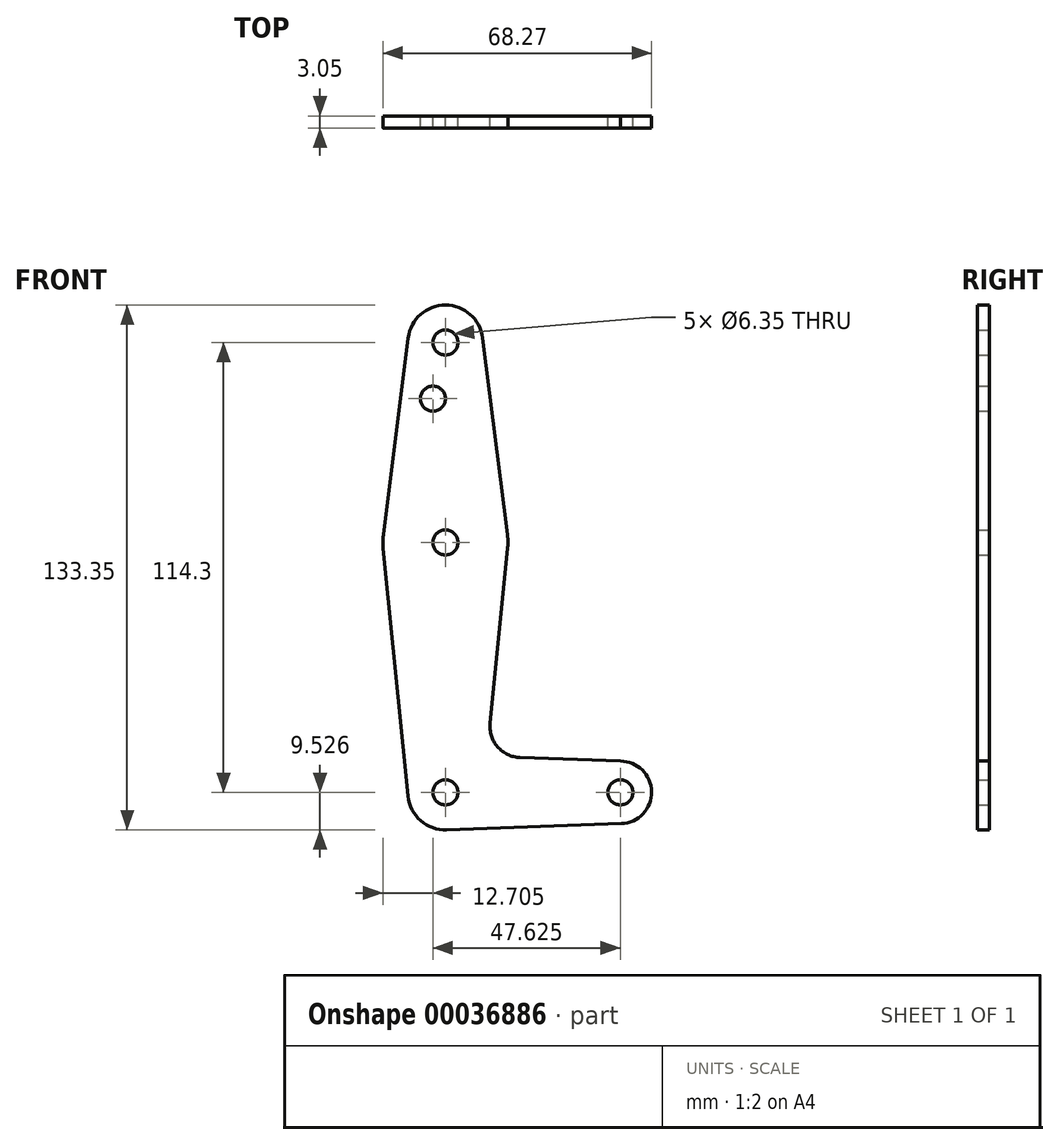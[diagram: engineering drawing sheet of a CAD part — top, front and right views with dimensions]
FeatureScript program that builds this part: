
annotation { "Feature Type Name" : "Feature", "Feature Type Description" : "" }
export const myFeature = defineFeature(function(context is Context, id is Id, definition is map)
    precondition{}
    {
        {
            var Q0;
            Q0=qCreatedBy(makeId("Front.planeOp"),FACE);
            var sketch = newSketch(context, id + "F0", { "sketchPlane" : qUnion([Q0])});
            skLineSegment(sketch, "E0", {"start": v(-44.45, 62.85) * mm, "end": v(-44.45, -51.45) * mm, "construction": true});
            skLineSegment(sketch, "E1", {"start": v(-44.45, -51.45) * mm, "end": v(0, -51.45) * mm, "construction": true});
            skCircle(sketch, "E2", {"center": v(-44.45, -51.45) * mm, "radius": 9.53 * mm});
            skCircle(sketch, "E3", {"center": v(0, -51.45) * mm, "radius": 7.94 * mm});
            skCircle(sketch, "E4", {"center": v(-44.45, 62.85) * mm, "radius": 9.53 * mm});
            skCircle(sketch, "E5", {"center": v(-44.45, 12.05) * mm, "radius": 15.88 * mm});
            skLineSegment(sketch, "E6", {"start": v(-60.25, 10.46) * mm, "end": v(-53.93, -52.4) * mm});
            skLineSegment(sketch, "E7", {"start": v(0, -43.52) * mm, "end": v(-25.48, -42.6) * mm});
            skLineSegment(sketch, "E8", {"start": v(-33.1, -33.86) * mm, "end": v(-28.65, 10.46) * mm});
            skLineSegment(sketch, "E9", {"start": v(-28.7, 14.03) * mm, "end": v(-35, 64.04) * mm});
            skLineSegment(sketch, "E10", {"start": v(-53.9, 64.04) * mm, "end": v(-60.2, 14.03) * mm});
            skCircle(sketch, "E11", {"center": v(-44.45, 62.85) * mm, "radius": 3.18 * mm});
            skCircle(sketch, "E12", {"center": v(-44.45, 12.05) * mm, "radius": 3.18 * mm});
            skCircle(sketch, "E13", {"center": v(-44.45, -51.45) * mm, "radius": 3.18 * mm});
            skCircle(sketch, "E14", {"center": v(0, -51.45) * mm, "radius": 3.18 * mm});
            skLineSegment(sketch, "E15", {"start": v(-44.1, -60.97) * mm, "end": v(0.28, -59.39) * mm});
            skCircle(sketch, "E16", {"center": v(-47.63, 48.57) * mm, "radius": 3.18 * mm});
            skArc(sketch, "E17.filletArc", {"start": v(-33.1, -33.86) * mm, "mid": v(-31.19, -39.88) * mm, "end": v(-25.48, -42.6) * mm});
            skSolve(sketch);
        }
        {
            var Q0;
            Q0 = qSketchRegion(id + "F0", true);
            extrude(context, id + "F1", {"entities" : qUnion([Q0]), "depth" : 3.05 * mm});
        }
    });
